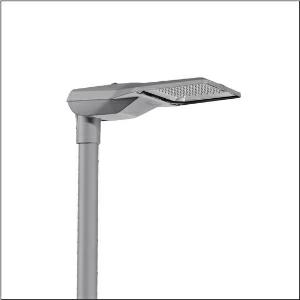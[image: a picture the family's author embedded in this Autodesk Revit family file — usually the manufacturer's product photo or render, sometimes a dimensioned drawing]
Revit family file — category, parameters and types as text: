
# Revit family: streetlight_sl_21_midi___st1_5a_5xe3p33s08mb_c1a7
name_source: partatom
category: Lighting Fixtures
units: mm (PartAtom-declared; Revit-internal decimal feet)

## family parameters
Cut with Voids When Loaded = No
Host = Face
Light Source = No
Part Type = Normal
Room Calculation Point = No
Round Connector Dimension = Use Diameter
Shared = No

## types (1)
- --- (1 x LED, 17960 lm, 136 W, 3000K)
    Apparent Load = 136 VA
    CIE Flux Codes = 22 53 95 100 100
    Color Rendering = 70
    Color Temperature = 3000K
    Default Elevation = 1800 mm
    Description = Streetlight SL 21 midi, mast luminaire, primary light control with lens, of PMMA, primary optical cover: cover, of toughened safety glass, transparent, light distribution: ST1.5a, light emission: direct distribution, primary light characteristic: asymmetric, installation type: side-entry, post-top, LED, High Power LED, rated luminous flux: 17.960lm, luminous efficacy: 132lm/W, light colour: 730, colour temperature: 3000K, control: overheat protection, constant luminous flux control, time-dependent luminous flux control, flexible luminous flux parameterisation, presetting dimming logarithmic, mains connection: 230..240V, AC, 50/60Hz, start of lifetime: 136W, end of service life: 142W, reduction: 61W, luminaire housing, of diecast aluminium, powder-coated, Siteco® metallic grey (DB 702S), corrosivity category C5 mid according to DIN EN ISO 12944, please order mast flange separately, inclination adjustable: 0°, 5°, 10°, 15°, sealing non-destructively replaceable, multi-level sealing system, length: 644mm, width: 335mm, height: 110mm, mast flange for spigot size: 42mm (side-entry): 5XC10008XM4, 60/48mm (side-entry/post-top): 5XC10108XM2, 76/60mm (side-entry/post-top): 5XC10108XM1, Smart Interface above, protection rating (complete): IP66, insulation class (complete): insulation class II (safety insulation), certification: CE, ENEC, ENEC+, VDE, impact resistance: IK09, permissible operating ambient temperature for outdoor applications: -40..+50°C, standard-compliant lighting for roads and squares, packaging unit: 1 piece

Light Distribution: ST1.5a
    Height = 111 mm
    Lamp = 1 x LED
    Lamp Light Flux = 17960 lm
    Lamp Power = 136 W
    Lamp count = 1
    Length = 644 mm
    Luminous efficacy = 132 lm/W
    Manufacturer = Siteco
    ModVariant = No
    Model = 5XE3P33S08MB
    Number of Poles = 1
    OnlyDefault = Yes
    Power Factor = 1
    Product Name = Streetlight SL 21 midi | ST1.5a
    Product group = mast luminaire | pylon top
    ProductGroupID = 6100
    Protection Class = Protection class II
    Protection Degree = IP 66
    RLX_Detail_Level = 1
    RLX_Emergency_Light_Flux = 0 lm
    RLX_Emergency_Type = 0
    RLX_Emergency_Type_DB = No
    RlxData = <blob elided: 95553 chars, md5=94415f47>
    Socket = socket
    Standby Power = 0 W
    System Light Flux = 17960 lm
    System Power = 136 W
    Type Comments = factory setting: luminous flux: 100 % | dim-lin: 254 | 695 mA
    Type Image = l_1004302.jpg
    URL = http://relux.com
    VarID = @adj_127261
    Voltage = 0 V
    Weight = 0.00 kg
    Width = 336 mm

## geometry (parser evidence)
native form markers: Blend x4, Sweep x9
no freeform markers — native parametric forms only
